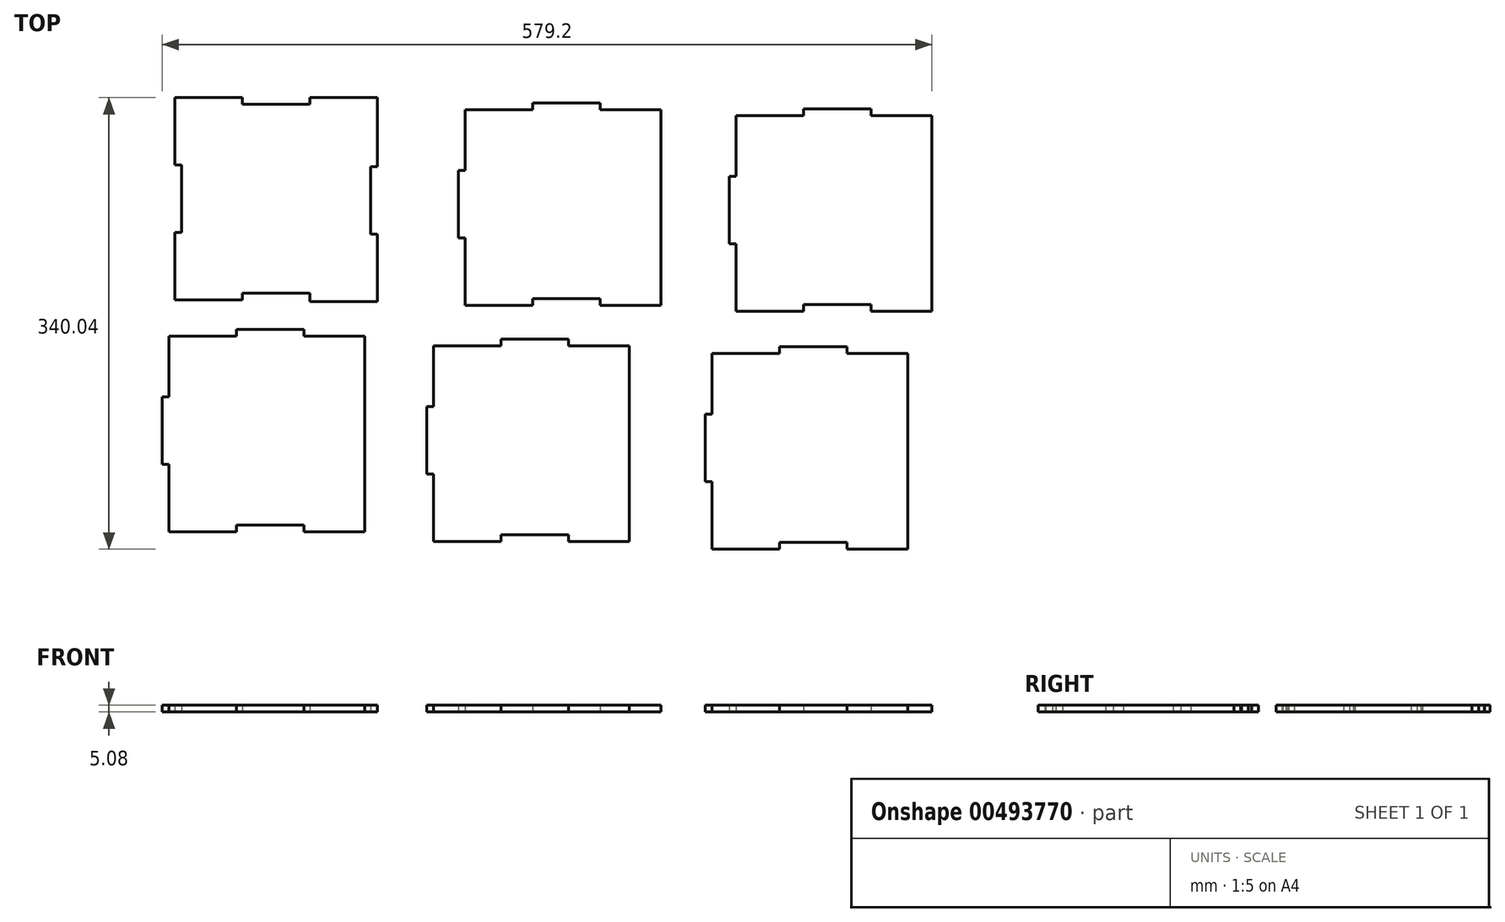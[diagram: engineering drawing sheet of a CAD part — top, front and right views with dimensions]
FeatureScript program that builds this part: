
annotation { "Feature Type Name" : "Feature", "Feature Type Description" : "" }
export const myFeature = defineFeature(function(context is Context, id is Id, definition is map)
    precondition{}
    {
        {
            var Q0;
            Q0=qCreatedBy(makeId("Top.planeOp"),FACE);
            var sketch = newSketch(context, id + "F0", { "sketchPlane" : qUnion([Q0])});
            skLineSegment(sketch, "E0.bottom", {"start": v(0, 101.6) * mm, "end": v(5.08, 101.6) * mm});
            skLineSegment(sketch, "E0.top", {"start": v(0, 50.8) * mm, "end": v(5.08, 50.8) * mm});
            skLineSegment(sketch, "E0.right", {"start": v(5.08, 101.6) * mm, "end": v(5.08, 50.8) * mm});
            skLineSegment(sketch, "E1.top", {"start": v(101.6, 5.08) * mm, "end": v(50.8, 5.08) * mm});
            skLineSegment(sketch, "E1.left", {"start": v(101.6, -1.27) * mm, "end": v(101.6, 5.08) * mm});
            skLineSegment(sketch, "E1.right", {"start": v(50.8, 0) * mm, "end": v(50.8, 5.08) * mm});
            skLineSegment(sketch, "E2", {"start": v(0, 152.4) * mm, "end": v(0, 101.6) * mm});
            skLineSegment(sketch, "E3", {"start": v(0, 0) * mm, "end": v(0, 50.8) * mm});
            skLineSegment(sketch, "E4", {"start": v(0, 152.4) * mm, "end": v(50.8, 152.4) * mm});
            skLineSegment(sketch, "E5", {"start": v(101.6, 152.4) * mm, "end": v(152.4, 152.4) * mm});
            skLineSegment(sketch, "E6", {"start": v(152.4, 152.4) * mm, "end": v(152.4, 100.33) * mm});
            skLineSegment(sketch, "E7", {"start": v(152.4, 49.53) * mm, "end": v(152.4, -1.27) * mm});
            skLineSegment(sketch, "E8", {"start": v(152.4, -1.27) * mm, "end": v(101.6, -1.27) * mm});
            skLineSegment(sketch, "E9", {"start": v(50.8, 0) * mm, "end": v(0, 0) * mm});
            skLineSegment(sketch, "E10", {"start": v(50.8, 152.4) * mm, "end": v(50.8, 147.32) * mm});
            skLineSegment(sketch, "E11", {"start": v(50.8, 147.32) * mm, "end": v(101.6, 147.32) * mm});
            skLineSegment(sketch, "E12", {"start": v(101.6, 147.32) * mm, "end": v(101.6, 152.4) * mm});
            skLineSegment(sketch, "E13", {"start": v(152.4, 100.33) * mm, "end": v(147.32, 100.33) * mm});
            skLineSegment(sketch, "E14", {"start": v(147.32, 100.33) * mm, "end": v(147.32, 49.53) * mm});
            skLineSegment(sketch, "E15", {"start": v(147.32, 49.53) * mm, "end": v(152.4, 49.53) * mm});
            skLineSegment(sketch, "E16", {"start": v(-4.4, -27.05) * mm, "end": v(-4.4, -72.77) * mm});
            skLineSegment(sketch, "E17", {"start": v(-4.4, -72.77) * mm, "end": v(-9.48, -72.77) * mm});
            skLineSegment(sketch, "E18", {"start": v(-9.48, -72.77) * mm, "end": v(-9.48, -123.57) * mm});
            skLineSegment(sketch, "E19", {"start": v(-9.48, -123.57) * mm, "end": v(-4.4, -123.57) * mm});
            skLineSegment(sketch, "E20", {"start": v(-4.4, -123.57) * mm, "end": v(-4.4, -174.37) * mm});
            skLineSegment(sketch, "E21", {"start": v(-4.4, -174.37) * mm, "end": v(46.4, -174.37) * mm});
            skLineSegment(sketch, "E22", {"start": v(46.4, -174.37) * mm, "end": v(46.4, -169.29) * mm});
            skLineSegment(sketch, "E23", {"start": v(46.4, -169.29) * mm, "end": v(97.2, -169.29) * mm});
            skLineSegment(sketch, "E24", {"start": v(97.2, -169.29) * mm, "end": v(97.2, -174.37) * mm});
            skLineSegment(sketch, "E25", {"start": v(97.2, -174.37) * mm, "end": v(142.92, -174.37) * mm});
            skLineSegment(sketch, "E26", {"start": v(142.92, -174.37) * mm, "end": v(142.92, -27.05) * mm});
            skLineSegment(sketch, "E27", {"start": v(142.92, -27.05) * mm, "end": v(97.2, -27.05) * mm});
            skLineSegment(sketch, "E28", {"start": v(97.2, -27.05) * mm, "end": v(97.2, -21.97) * mm});
            skLineSegment(sketch, "E29", {"start": v(97.2, -21.97) * mm, "end": v(46.4, -21.97) * mm});
            skLineSegment(sketch, "E30", {"start": v(46.4, -21.97) * mm, "end": v(46.4, -27.05) * mm});
            skLineSegment(sketch, "E31", {"start": v(46.4, -27.05) * mm, "end": v(-4.4, -27.05) * mm});
            skLineSegment(sketch, "E32", {"start": v(218.66, 143.2) * mm, "end": v(218.66, 97.48) * mm});
            skLineSegment(sketch, "E33", {"start": v(218.66, 97.48) * mm, "end": v(213.58, 97.48) * mm});
            skLineSegment(sketch, "E34", {"start": v(213.58, 97.48) * mm, "end": v(213.58, 46.68) * mm});
            skLineSegment(sketch, "E35", {"start": v(213.58, 46.68) * mm, "end": v(218.66, 46.68) * mm});
            skLineSegment(sketch, "E36", {"start": v(218.66, 46.68) * mm, "end": v(218.66, -4.12) * mm});
            skLineSegment(sketch, "E37", {"start": v(218.66, -4.12) * mm, "end": v(269.46, -4.12) * mm});
            skLineSegment(sketch, "E38", {"start": v(269.46, -4.12) * mm, "end": v(269.46, 0.96) * mm});
            skLineSegment(sketch, "E39", {"start": v(269.46, 0.96) * mm, "end": v(320.26, 0.96) * mm});
            skLineSegment(sketch, "E40", {"start": v(320.26, 0.96) * mm, "end": v(320.26, -4.12) * mm});
            skLineSegment(sketch, "E41", {"start": v(320.26, -4.12) * mm, "end": v(365.98, -4.12) * mm});
            skLineSegment(sketch, "E42", {"start": v(365.98, -4.12) * mm, "end": v(365.98, 143.2) * mm});
            skLineSegment(sketch, "E43", {"start": v(365.98, 143.2) * mm, "end": v(320.26, 143.2) * mm});
            skLineSegment(sketch, "E44", {"start": v(320.26, 143.2) * mm, "end": v(320.26, 148.28) * mm});
            skLineSegment(sketch, "E45", {"start": v(320.26, 148.28) * mm, "end": v(269.46, 148.28) * mm});
            skLineSegment(sketch, "E46", {"start": v(269.46, 148.28) * mm, "end": v(269.46, 143.2) * mm});
            skLineSegment(sketch, "E47", {"start": v(269.46, 143.2) * mm, "end": v(218.66, 143.2) * mm});
            skLineSegment(sketch, "E48", {"start": v(194.82, -34.54) * mm, "end": v(194.82, -80.26) * mm});
            skLineSegment(sketch, "E49", {"start": v(194.82, -80.26) * mm, "end": v(189.74, -80.26) * mm});
            skLineSegment(sketch, "E50", {"start": v(189.74, -80.26) * mm, "end": v(189.74, -131.06) * mm});
            skLineSegment(sketch, "E51", {"start": v(189.74, -131.06) * mm, "end": v(194.82, -131.06) * mm});
            skLineSegment(sketch, "E52", {"start": v(194.82, -131.06) * mm, "end": v(194.82, -181.86) * mm});
            skLineSegment(sketch, "E53", {"start": v(194.82, -181.86) * mm, "end": v(245.62, -181.86) * mm});
            skLineSegment(sketch, "E54", {"start": v(245.62, -181.86) * mm, "end": v(245.62, -176.78) * mm});
            skLineSegment(sketch, "E55", {"start": v(245.62, -176.78) * mm, "end": v(296.42, -176.78) * mm});
            skLineSegment(sketch, "E56", {"start": v(296.42, -176.78) * mm, "end": v(296.42, -181.86) * mm});
            skLineSegment(sketch, "E57", {"start": v(296.42, -181.86) * mm, "end": v(342.14, -181.86) * mm});
            skLineSegment(sketch, "E58", {"start": v(342.14, -181.86) * mm, "end": v(342.14, -34.54) * mm});
            skLineSegment(sketch, "E59", {"start": v(342.14, -34.54) * mm, "end": v(296.42, -34.54) * mm});
            skLineSegment(sketch, "E60", {"start": v(296.42, -34.54) * mm, "end": v(296.42, -29.46) * mm});
            skLineSegment(sketch, "E61", {"start": v(296.42, -29.46) * mm, "end": v(245.62, -29.46) * mm});
            skLineSegment(sketch, "E62", {"start": v(245.62, -29.46) * mm, "end": v(245.62, -34.54) * mm});
            skLineSegment(sketch, "E63", {"start": v(245.62, -34.54) * mm, "end": v(194.82, -34.54) * mm});
            skLineSegment(sketch, "E64", {"start": v(422.4, 138.87) * mm, "end": v(422.4, 93.15) * mm});
            skLineSegment(sketch, "E65", {"start": v(422.4, 93.15) * mm, "end": v(417.32, 93.15) * mm});
            skLineSegment(sketch, "E66", {"start": v(417.32, 93.15) * mm, "end": v(417.32, 42.35) * mm});
            skLineSegment(sketch, "E67", {"start": v(417.32, 42.35) * mm, "end": v(422.4, 42.35) * mm});
            skLineSegment(sketch, "E68", {"start": v(422.4, 42.35) * mm, "end": v(422.4, -8.45) * mm});
            skLineSegment(sketch, "E69", {"start": v(422.4, -8.45) * mm, "end": v(473.2, -8.45) * mm});
            skLineSegment(sketch, "E70", {"start": v(473.2, -8.45) * mm, "end": v(473.2, -3.37) * mm});
            skLineSegment(sketch, "E71", {"start": v(473.2, -3.37) * mm, "end": v(524, -3.37) * mm});
            skLineSegment(sketch, "E72", {"start": v(524, -3.37) * mm, "end": v(524, -8.45) * mm});
            skLineSegment(sketch, "E73", {"start": v(524, -8.45) * mm, "end": v(569.72, -8.45) * mm});
            skLineSegment(sketch, "E74", {"start": v(569.72, -8.45) * mm, "end": v(569.72, 138.87) * mm});
            skLineSegment(sketch, "E75", {"start": v(569.72, 138.87) * mm, "end": v(524, 138.87) * mm});
            skLineSegment(sketch, "E76", {"start": v(524, 138.87) * mm, "end": v(524, 143.95) * mm});
            skLineSegment(sketch, "E77", {"start": v(524, 143.95) * mm, "end": v(473.2, 143.95) * mm});
            skLineSegment(sketch, "E78", {"start": v(473.2, 143.95) * mm, "end": v(473.2, 138.87) * mm});
            skLineSegment(sketch, "E79", {"start": v(473.2, 138.87) * mm, "end": v(422.4, 138.87) * mm});
            skLineSegment(sketch, "E80", {"start": v(404.34, -40.32) * mm, "end": v(404.34, -86.04) * mm});
            skLineSegment(sketch, "E81", {"start": v(404.34, -86.04) * mm, "end": v(399.26, -86.04) * mm});
            skLineSegment(sketch, "E82", {"start": v(399.26, -86.04) * mm, "end": v(399.26, -136.84) * mm});
            skLineSegment(sketch, "E83", {"start": v(399.26, -136.84) * mm, "end": v(404.34, -136.84) * mm});
            skLineSegment(sketch, "E84", {"start": v(404.34, -136.84) * mm, "end": v(404.34, -187.64) * mm});
            skLineSegment(sketch, "E85", {"start": v(404.34, -187.64) * mm, "end": v(455.14, -187.64) * mm});
            skLineSegment(sketch, "E86", {"start": v(455.14, -187.64) * mm, "end": v(455.14, -182.56) * mm});
            skLineSegment(sketch, "E87", {"start": v(455.14, -182.56) * mm, "end": v(505.94, -182.56) * mm});
            skLineSegment(sketch, "E88", {"start": v(505.94, -182.56) * mm, "end": v(505.94, -187.64) * mm});
            skLineSegment(sketch, "E89", {"start": v(505.94, -187.64) * mm, "end": v(551.66, -187.64) * mm});
            skLineSegment(sketch, "E90", {"start": v(551.66, -187.64) * mm, "end": v(551.66, -40.32) * mm});
            skLineSegment(sketch, "E91", {"start": v(551.66, -40.32) * mm, "end": v(505.94, -40.32) * mm});
            skLineSegment(sketch, "E92", {"start": v(505.94, -40.32) * mm, "end": v(505.94, -35.24) * mm});
            skLineSegment(sketch, "E93", {"start": v(505.94, -35.24) * mm, "end": v(455.14, -35.24) * mm});
            skLineSegment(sketch, "E94", {"start": v(455.14, -35.24) * mm, "end": v(455.14, -40.32) * mm});
            skLineSegment(sketch, "E95", {"start": v(455.14, -40.32) * mm, "end": v(404.34, -40.32) * mm});
            skSolve(sketch);
        }
        {
            var Q0;
            Q0=makeQuery(id+"F0.imprint","IMPRINT",FACE,{"disambiguationData":[TD([[makeQuery(id+"F0.imprint","IMPRINT",EDGE,{"derivedFrom":sQuery(id+"F0.wireOp",EDGE,"E0.bottom")}),1.0]])]});
            var Q1;
            Q1=makeQuery(id+"F0.imprint","IMPRINT",FACE,{"disambiguationData":[TD([[makeQuery(id+"F0.imprint","IMPRINT",EDGE,{"derivedFrom":sQuery(id+"F0.wireOp",EDGE,"lCVuTxi1-wZ5Z-coNt-Hn01-GH8afqEx9Zw5")}),1.0]])]});
            var Q2;
            Q2=makeQuery(id+"F0.imprint","IMPRINT",FACE,{"disambiguationData":[TD([[makeQuery(id+"F0.imprint","IMPRINT",EDGE,{"derivedFrom":sQuery(id+"F0.wireOp",EDGE,"bcea0751-7caa-4bb8-941f-46de89519f09")}),1.0]])]});
            var Q3;
            Q3=makeQuery(id+"F0.imprint","IMPRINT",FACE,{"disambiguationData":[TD([[makeQuery(id+"F0.imprint","IMPRINT",EDGE,{"derivedFrom":sQuery(id+"F0.wireOp",EDGE,"d6dcac8e-6497-4386-8271-9a9ff3424b1f")}),1.0]])]});
            var Q4;
            Q4=makeQuery(id+"F0.imprint","IMPRINT",FACE,{"disambiguationData":[TD([[makeQuery(id+"F0.imprint","IMPRINT",EDGE,{"derivedFrom":sQuery(id+"F0.wireOp",EDGE,"fde45935-d408-44a5-8a0c-06697c315eb7")}),1.0]])]});
            var Q5;
            Q5=makeQuery(id+"F0.imprint","IMPRINT",FACE,{"disambiguationData":[TD([[makeQuery(id+"F0.imprint","IMPRINT",EDGE,{"derivedFrom":sQuery(id+"F0.wireOp",EDGE,"E16")}),1.0]])]});
            var Q6;
            Q6=makeQuery(id+"F0.imprint","IMPRINT",FACE,{"disambiguationData":[TD([[makeQuery(id+"F0.imprint","IMPRINT",EDGE,{"derivedFrom":sQuery(id+"F0.wireOp",EDGE,"E32")}),1.0]])]});
            var Q7;
            Q7=makeQuery(id+"F0.imprint","IMPRINT",FACE,{"disambiguationData":[TD([[makeQuery(id+"F0.imprint","IMPRINT",EDGE,{"derivedFrom":sQuery(id+"F0.wireOp",EDGE,"E64")}),1.0]])]});
            var Q8;
            Q8=makeQuery(id+"F0.imprint","IMPRINT",FACE,{"disambiguationData":[TD([[makeQuery(id+"F0.imprint","IMPRINT",EDGE,{"derivedFrom":sQuery(id+"F0.wireOp",EDGE,"E80")}),1.0]])]});
            var Q9;
            Q9=makeQuery(id+"F0.imprint","IMPRINT",FACE,{"disambiguationData":[TD([[makeQuery(id+"F0.imprint","IMPRINT",EDGE,{"derivedFrom":sQuery(id+"F0.wireOp",EDGE,"E48")}),1.0]])]});
            extrude(context, id + "F1", {"entities" : qUnion([Q0, Q1, Q2, Q3, Q4, Q5, Q6, Q7, Q8, Q9]), "depth" : 5.08 * mm, "offsetDistance" : 25.4 * mm});
        }
    });
